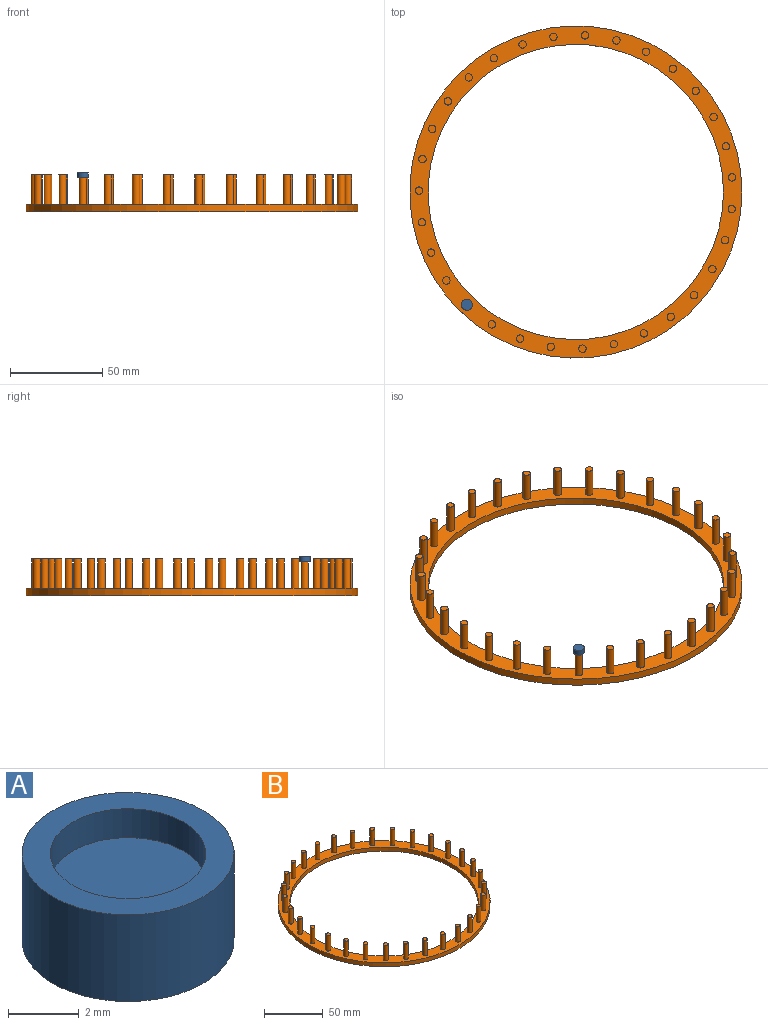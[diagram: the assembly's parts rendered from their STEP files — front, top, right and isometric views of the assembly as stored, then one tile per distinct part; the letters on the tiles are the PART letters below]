
ASSEMBLY  parts=2 mates=1
PART A: 5 faces, bbox 6x6x3 mm
  f0: cylinder r=2.2mm len=4.4mm, axis (0,0,-1), area 13.8mm2, adj f2,f4
  f1: cylinder r=3mm len=6mm, axis (0,0,-1), area 56.5mm2, adj f2,f3
  f2: plane 6x6mm, normal (0,0,1), area 13.1mm2, adj f0,f1
  f3: plane 6x6mm, normal (0,0,-1), area 28.3mm2, adj f1
  f4: plane 4.4x4.4mm, normal (0,0,1), area 15.2mm2, adj f0
PART B: 66 faces, bbox 180x180x20 mm
  f0: cylinder r=80mm len=160mm, axis (0,0,-1), area 2010.6mm2, adj f2,f3
  f1: cylinder r=90mm len=180mm, axis (0,0,-1), area 2261.9mm2, adj f2,f3
  f2: plane 180x180mm, normal (0,0,1), area 4951.2mm2, adj f0,f1,f4,f6,f8,f10,f12,f14
  f3: plane 180x180mm, normal (0,0,-1), area 5340.7mm2, adj f0,f1
  f4: cylinder r=2mm len=16mm, axis (0,0,-1), area 201.1mm2, adj f2,f5
  f5: plane 4x4mm, normal (0,0,1), area 12.6mm2, adj f4
  f6: cylinder r=2mm len=16mm, axis (0,0,-1), area 201.1mm2, adj f2,f7
  f7: plane 4x4mm, normal (0,0,1), area 12.6mm2, adj f6
  f8: cylinder r=2mm len=16mm, axis (0,0,-1), area 201.1mm2, adj f2,f9
  f9: plane 4x4mm, normal (0,0,1), area 12.6mm2, adj f8
  f10: cylinder r=2mm len=16mm, axis (0,0,-1), area 201.1mm2, adj f2,f11
  f11: plane 4x4mm, normal (0,0,1), area 12.6mm2, adj f10
  f12: cylinder r=2mm len=16mm, axis (0,0,-1), area 201.1mm2, adj f2,f13
  f13: plane 4x4mm, normal (0,0,1), area 12.6mm2, adj f12
  f14: cylinder r=2mm len=16mm, axis (0,0,-1), area 201.1mm2, adj f2,f15
  f15: plane 4x4mm, normal (0,0,1), area 12.6mm2, adj f14
  f16: cylinder r=2mm len=16mm, axis (0,0,-1), area 201.1mm2, adj f2,f17
  f17: plane 4x4mm, normal (0,0,1), area 12.6mm2, adj f16
  f18: cylinder r=2mm len=16mm, axis (0,0,-1), area 201.1mm2, adj f2,f19
  f19: plane 4x4mm, normal (0,0,1), area 12.6mm2, adj f18
  f20: cylinder r=2mm len=16mm, axis (0,0,-1), area 201.1mm2, adj f2,f21
  f21: plane 4x4mm, normal (0,0,1), area 12.6mm2, adj f20
  f22: cylinder r=2mm len=16mm, axis (0,0,-1), area 201.1mm2, adj f2,f23
  f23: plane 4x4mm, normal (0,0,1), area 12.6mm2, adj f22
  f24: cylinder r=2mm len=16mm, axis (0,0,-1), area 201.1mm2, adj f2,f25
  f25: plane 4x4mm, normal (0,0,1), area 12.6mm2, adj f24
  f26: cylinder r=2mm len=16mm, axis (0,0,-1), area 201.1mm2, adj f2,f27
  f27: plane 4x4mm, normal (0,0,1), area 12.6mm2, adj f26
  f28: cylinder r=2mm len=16mm, axis (0,0,-1), area 201.1mm2, adj f2,f29
  f29: plane 4x4mm, normal (0,0,1), area 12.6mm2, adj f28
  f30: cylinder r=2mm len=16mm, axis (0,0,-1), area 201.1mm2, adj f2,f31
  f31: plane 4x4mm, normal (0,0,1), area 12.6mm2, adj f30
  f32: cylinder r=2mm len=16mm, axis (0,0,-1), area 201.1mm2, adj f2,f33
  f33: plane 4x4mm, normal (0,0,1), area 12.6mm2, adj f32
  f34: cylinder r=2mm len=16mm, axis (0,0,-1), area 201.1mm2, adj f2,f35
  f35: plane 4x4mm, normal (0,0,1), area 12.6mm2, adj f34
  f36: cylinder r=2mm len=16mm, axis (0,0,-1), area 201.1mm2, adj f2,f37
  f37: plane 4x4mm, normal (0,0,1), area 12.6mm2, adj f36
  f38: cylinder r=2mm len=16mm, axis (0,0,-1), area 201.1mm2, adj f2,f39
  f39: plane 4x4mm, normal (0,0,1), area 12.6mm2, adj f38
  f40: cylinder r=2mm len=16mm, axis (0,0,-1), area 201.1mm2, adj f2,f41
  f41: plane 4x4mm, normal (0,0,1), area 12.6mm2, adj f40
  f42: cylinder r=2mm len=16mm, axis (0,0,-1), area 201.1mm2, adj f2,f43
  f43: plane 4x4mm, normal (0,0,1), area 12.6mm2, adj f42
  f44: cylinder r=2mm len=16mm, axis (0,0,-1), area 201.1mm2, adj f2,f45
  f45: plane 4x4mm, normal (0,0,1), area 12.6mm2, adj f44
  f46: cylinder r=2mm len=16mm, axis (0,0,-1), area 201.1mm2, adj f2,f47
  f47: plane 4x4mm, normal (0,0,1), area 12.6mm2, adj f46
  f48: cylinder r=2mm len=16mm, axis (0,0,-1), area 201.1mm2, adj f2,f49
  f49: plane 4x4mm, normal (0,0,1), area 12.6mm2, adj f48
  f50: cylinder r=2mm len=16mm, axis (0,0,-1), area 201.1mm2, adj f2,f51
  f51: plane 4x4mm, normal (0,0,1), area 12.6mm2, adj f50
  f52: cylinder r=2mm len=16mm, axis (0,0,-1), area 201.1mm2, adj f2,f53
  f53: plane 4x4mm, normal (0,0,1), area 12.6mm2, adj f52
  f54: cylinder r=2mm len=16mm, axis (0,0,-1), area 201.1mm2, adj f2,f55
  f55: plane 4x4mm, normal (0,0,1), area 12.6mm2, adj f54
  f56: cylinder r=2mm len=16mm, axis (0,0,-1), area 201.1mm2, adj f2,f57
  f57: plane 4x4mm, normal (0,0,1), area 12.6mm2, adj f56
  f58: cylinder r=2mm len=16mm, axis (0,0,-1), area 201.1mm2, adj f2,f59
  f59: plane 4x4mm, normal (0,0,1), area 12.6mm2, adj f58
  f60: cylinder r=2mm len=16mm, axis (0,0,-1), area 201.1mm2, adj f2,f61
  f61: plane 4x4mm, normal (0,0,1), area 12.6mm2, adj f60
  f62: cylinder r=2mm len=16mm, axis (0,0,-1), area 201.1mm2, adj f2,f63
  f63: plane 4x4mm, normal (0,0,1), area 12.6mm2, adj f62
  f64: cylinder r=2mm len=16mm, axis (0,0,-1), area 201.1mm2, adj f2,f65
  f65: plane 4x4mm, normal (0,0,1), area 12.6mm2, adj f64
PLACE A rot(axis=(0,1,0),180deg) t=(-59.67,-76.04,7.19)mm
PLACE B rot(axis=(0,1,0),0deg) t=(-0.6,-14.92,-14.31)mm
MATE fastened B.f16 <-> A.f1  axis (0,0,1) through (-59.67,-76.04,5.69)mm
